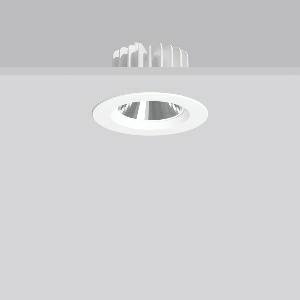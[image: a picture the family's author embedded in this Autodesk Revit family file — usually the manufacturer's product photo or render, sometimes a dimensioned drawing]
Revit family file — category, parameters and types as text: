
# Revit family: ledona_round_ip20_901791_002_76_5911
name_source: partatom
category: Lighting Fixtures
units: mm (PartAtom-declared; Revit-internal decimal feet)

## family parameters
Cut with Voids When Loaded = No
Host = Face
Light Source = No
Part Type = Normal
Room Calculation Point = No
Round Connector Dimension = Use Diameter
Shared = No

## types (1)
- MultiLumen 1 (1 x LED Modul 930, 1500 lm, 3000)
    Apparent Load = 12 VA
    Approval mark = CE
    CIE Flux Codes = 96 100 100 100 100
    Color Rendering = 90
    Color Temperature = 3000
    Default Elevation = 1800 mm
    Description = Series: LEDONA round
Recessed LED downlight featuring advanced technology and sophisticated design. Housing: die-cast aluminium constructed as heat sink.Bezel ring: die-cast aluminium, powder-coated. Open version. Highly polished four-segment faceted aluminium reflector with light mixing chamber. MultiLumen: Luminous flux adjustable in different steps. Best colour rendering index Ra>90. Installation without tools thanks to spring fastening system. Connected converter included in separate gearbox. With connecting cable (L 250 mm). Suitable for through wiring as standard. 
Colour: white
Diameter: 140 mm
Height: 3 mm
Cut-out diameter: 120 mm
Recess height: 79 mm
Luminaire: recess height: 79 mm
Lamp: LED
Socket: without socket
Colour temperature: 3000K
Colour rendering index (CRI): 90
System power: 12 W
Rated luminous flux: 1500 lm
Luminous efficiency: 125 lm/W
System power 2: 16 W
Rated luminous flux 2: 1950 lm
Luminous efficiency 2: 122 lm/W
System power 3: 19 W
Rated luminous flux 3: 2400 lm
Luminous efficiency 3: 126 lm/W
System power 4: 25 W
Rated luminous flux 4: 3000 lm
Luminous efficiency 4: 120 lm/W
Control gear: Converter, dimmable, DALI
Protection class: II
Type of protection: IP 20
    Height = 0 mm  [stored 0 ft]
    Lamp = 1 x LED Modul 930
    Lamp Light Flux = 1500 lm
    Lamp count = 1
    Length = 140 mm  [stored 0.459318 ft]
    Lifetime = 50000 h
    Luminous efficacy = 125 lm/W
    Manufacturer = RZB
    ModVariant = No
    Model = 901791.002.76
    Mounting Place = Ceiling
    Mounting Type = Recessed
    Number of Poles = 1
    OnlyDefault = Yes
    Power Factor = 1
    Product Name = LEDONA round IP20
    Product group = Recessed downlights
    ProductGroupID = 402
    Protection Class = Protection class II
    Protection Degree = IP 20
    RLX_Detail_Level = 1
    RLX_Emergency_Light_Flux = 0 lm
    RLX_Emergency_Type = 0
    RLX_Emergency_Type_DB = No
    RlxData = <blob elided: 34697 chars, md5=5370bf06>
    Socket = socket
    Standby Power = 0 W
    System Light Flux = 1500 lm
    System Power = 12 W
    Type Comments = MultiLumen 1
    Type Image = 901383.002.jpg
    URL = http://relux.com
    VarID = multilumen_1
    Voltage = 230 V
    Voltage Range = 220-240 V
    Weight = 0.00 kg
    Width = 0 mm  [stored 0 ft]

note: [stored X ft] marks values corroborated as IEEE doubles in the binary element streams (Revit-internal decimal feet)

## geometry (parser evidence)
native form markers: Blend x4, Sweep x8
no freeform markers — native parametric forms only
